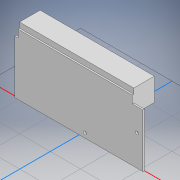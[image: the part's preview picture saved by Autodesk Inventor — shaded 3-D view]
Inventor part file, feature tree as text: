
AUTODESK INVENTOR PART (.ipt)
format: ipt  version: 2022 (Build 260153000, 153)  size: 131,584 bytes
history: native  units: mm
features: extrude x3, sketch x3, other x1
ambient origin geometry x8: Origin, YZ Plane, XZ Plane, XY Plane, X Axis, Y Axis, Z Axis, Center Point
bodies: Body1 (feature_tree)
feature tree (7):
  other  "Твердое тело1"
  extrude  "Выдавливание1"  Depth=84.0mm
  extrude  "Выдавливание2"  Depth=40.0mm
  extrude  "Выдавливание3"  Depth=5.0mm
  sketch  "Эскиз1"
  sketch  "Эскиз2"
  sketch  "Эскиз3"
